# Revit family: RN 90087 Optifitt-Serra-Vis de rappel
name_source: partatom
category: Rohrformteile
units: mm (PartAtom-declared; Revit-internal decimal feet)

## family parameters
Arbeitsebenenbasiert = Nein
Beim Laden mit Abzugskörper schneiden = Nein
Bemaßung runder Anschluss = Durchmesser verwenden
Gemeinsam genutzt = Nein
Immer vertikal = Ja
Teiletyp = Verbindung

## types (6) — shared parameters
1.010.00.2 Blattnummer der Richtlinie = 29
1.010.00.3 Ausgabedatum (Monat) der Richtlinie = 201308
1.010.00.4 Herstellername = R. Nussbaum AG
1.010.00.5 Revisionsdatum der Datei = 20190521
1.010.00.6 Webadresse des Herstellers = http://www.nussbaum.ch
1.100.00.4 Produktbezeichnung = Versorgung
1.110.00.2 Index = 3
1.110.00.4 Produktbezeichnung = Optifitt-Serra
1.960/3L.00.8 Link (URL) = https://www.nussbaum.ch
29.700.00.4 Produktname = Optifitt-Serra-Verschraubung, mit Aussengewinde, Dichtung PTFE
29.700.00.5 Produktkennung = 2
29.700.00.6 Querschnittsform = 1
29.700.00.7 Nennweitensystem = DN
29.700.00.8 Nenndrucksystem = PN
29.710.02.4 Nenndruck = 16
29.710.02.5 max. zul. Überdruck [hPa] = 1600
29.710.02.7 max. zul. Dauer-Betriebsdruck [hPa] = 1600
29.710.02.9 max. zul. Dauer-Betriebstemperatur [°C] = 90
Connector Visibility = Nein
EnclosingSpace Visibility = Nein
Hersteller = R. Nussbaum AG
URL = https://www.nussbaum.ch

## per-type parameters (varying)
| type | 1.800.00.3 TGA-Nummer | 1.800.00.4 Kommentarfeld | 1.810.00.3 Hersteller-Bestellnummer | 1.810.00.4 DATANORM-Nummer | 1.810.00.5 StLB-Nummer | 1.810.00.6 GTIN-Nummer | 29.710.02.10 Formstück-Gewicht [kg] | 29.710.02.3 Benennung | CONNECTOR0_DIAMETER_dX_0r | CONNECTOR0_dX_01 | CONNECTOR0_ref_dX | CONNECTOR1_DIAMETER_dX_0r | CONNECTOR1_dX_00 | CONNECTOR1_dX_01 | CONNECTOR1_ref_dX | Modell | R. Nussbaum AG 90087.04 de Visibility | R. Nussbaum AG 90087.05 de Visibility | R. Nussbaum AG 90087.06 de Visibility | R. Nussbaum AG 90087.07 de Visibility | R. Nussbaum AG 90087.08 de Visibility | R. Nussbaum AG 90087.09 de Visibility | Typenkommentare |
| DN=50 | 01900300000000000000000000000000000000000000000032000000000000000006 | 90087.09, Optifitt-Serra-Verschraubung, mit Aussengewinde, Dichtung PTFE, DN=50, L=95, R=2, Rp=2 | 90087.09 | 90087.09 | 215.217 | 7612945679987 | 1.453 | Optifitt-Serra-Verschraubung, mit Aussengewinde, Dichtung PTFE, DN=50, L=95, R=2, Rp=2 | 50 mm  [stored 0.164042 ft] | 24 mm | 24 mm | 50 mm  [stored 0.164042 ft] | 78 mm | 102 mm | 102 mm | 90087.09 | Nein | Nein | Nein | Nein | Nein | Ja | Optifitt-Serra-Vis de rappel  DN=50 |
| DN=40 | 01900300000000000000000000000000000000000000000032000000000000000005 | 90087.08, Optifitt-Serra-Verschraubung, mit Aussengewinde, Dichtung PTFE, DN=40, L=88, R=1½, Rp=1½ | 90087.08 | 90087.08 | 215.216 | 7612945679970 | 0.93 | Optifitt-Serra-Verschraubung, mit Aussengewinde, Dichtung PTFE, DN=40, L=88, R=1½, Rp=1½ | 40 mm | 19 mm | 19 mm | 40 mm | 76 mm | 95 mm | 95 mm | 90087.08 | Nein | Nein | Nein | Nein | Ja | Nein | Optifitt-Serra-Vis de rappel  DN=40 |
| DN=32 | 01900300000000000000000000000000000000000000000032000000000000000004 | 90087.07, Optifitt-Serra-Verschraubung, mit Aussengewinde, Dichtung PTFE, DN=32, L=83, R=1¼, Rp=1¼ | 90087.07 | 90087.07 | 215.215 | 7612945679963 | 0.846 | Optifitt-Serra-Verschraubung, mit Aussengewinde, Dichtung PTFE, DN=32, L=83, R=1¼, Rp=1¼ | 32 mm  [stored 0.104987 ft] | 19 mm | 19 mm | 32 mm  [stored 0.104987 ft] | 62 mm | 81 mm | 81 mm | 90087.07 | Nein | Nein | Nein | Ja | Nein | Nein | Optifitt-Serra-Vis de rappel  DN=32 |
| DN=25 | 01900300000000000000000000000000000000000000000032000000000000000003 | 90087.06, Optifitt-Serra-Verschraubung, mit Aussengewinde, Dichtung PTFE, DN=25, L=71, R=1, Rp=1 | 90087.06 | 90087.06 | 215.214 | 7612945679956 | 0.378 | Optifitt-Serra-Verschraubung, mit Aussengewinde, Dichtung PTFE, DN=25, L=71, R=1, Rp=1 | 25 mm  [stored 0.082021 ft] | 17 mm | 17 mm | 25 mm  [stored 0.082021 ft] | 54 mm | 71 mm | 71 mm | 90087.06 | Nein | Nein | Ja | Nein | Nein | Nein | Optifitt-Serra-Vis de rappel  DN=25 |
| DN=20 | 01900300000000000000000000000000000000000000000032000000000000000002 | 90087.05, Optifitt-Serra-Verschraubung, mit Aussengewinde, Dichtung PTFE, DN=20, L=65, R=¾, Rp=¾ | 90087.05 | 90087.05 | 215.213 | 7612945679949 | 0.304 | Optifitt-Serra-Verschraubung, mit Aussengewinde, Dichtung PTFE, DN=20, L=65, R=¾, Rp=¾ | 20 mm | 15 mm | 15 mm | 20 mm | 50 mm  [stored 0.164042 ft] | 65 mm | 65 mm | 90087.05 | Nein | Ja | Nein | Nein | Nein | Nein | Optifitt-Serra-Vis de rappel  DN=20 |
| DN=15 | 01900300000000000000000000000000000000000000000032000000000000000001 | 90087.04, Optifitt-Serra-Verschraubung, mit Aussengewinde, Dichtung PTFE, DN=15, L=62, R=½, Rp=½ | 90087.04 | 90087.04 | 215.212 | 7612945679932 | 0.231 | Optifitt-Serra-Verschraubung, mit Aussengewinde, Dichtung PTFE, DN=15, L=62, R=½, Rp=½ | 15 mm | 13 mm | 13 mm | 15 mm | 49 mm  [stored 0.160761 ft] | 62 mm | 62 mm | 90087.04 | Ja | Nein | Nein | Nein | Nein | Nein | Optifitt-Serra-Vis de rappel  DN=15 |

note: [stored X ft] marks values corroborated as IEEE doubles in the binary element streams (Revit-internal decimal feet)

## geometry (parser evidence)
native form markers: Sweep x2
no freeform markers — native parametric forms only
